# Revit family: Shower-Handshower_Kit-KOHLER-AVID-K-97386T
name_source: partatom
category: Plumbing Fixtures
revit_build: Autodesk Revit 2017 (Build: 20160225_1515(x64)
units: mm (PartAtom-declared; Revit-internal decimal feet)

## family parameters
Cut with Voids When Loaded = No
Host = Face
OmniClass Number = 23.31.17.00
OmniClass Title = Showers
Part Type = Normal
Room Calculation Point = No
Round Connector Dimension = Use Diameter
Shared = No

## types (2) — shared parameters
ADA Compliant = No
Assembly Code = D2010700
CW Connection = Yes
Cold Water Inlet = Cold Water Inlet
Date Modified = 11/27/2020
Description = Wall-mounted thermostatic bathtub shower faucet
Drain Included = No
Flow Rate = 2 GPM
HW Connection = Yes
Height = 28 5/16"
Hot Water Inlet = Hot Water Inlet
Length = 4 5/8"
Manufacturer = KOHLER Co.
Master Format 2014 = 22 42 23
Master Format 2014 Name = Residential Showers
Material = Premium Metal Construction
Pressure = 45.00 psi
Product Documentation Link = https://files.kohler.com.cn
Product Name = AVID
Product Page URL = https://www.kohler.com.cn
Spout Reach = 8 7/8"
URL = http://www.kohler.com.cn
Vent Connection = No
Waste Connection = No
Waste Water Outlet = Waste Water Outlet
WaterSense Certified = No
Width = 12 13/16"

## per-type parameters (varying)
| type | Default Elevation | Finish | Model | Type |
| CP-Polished Chrome | 36" | Kohler-Metal-CP-Polished_Chrome | K-97386T-9-CP | 1 |
| TT-Titanium Silver | 42" | Kohler-Metal-TT-Vibrant_Titanium | K-97386T-9-TT | 2 |

## geometry (parser evidence)
native form markers: Sweep x5
no freeform markers — native parametric forms only
